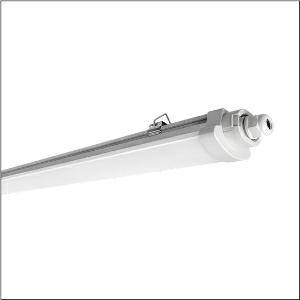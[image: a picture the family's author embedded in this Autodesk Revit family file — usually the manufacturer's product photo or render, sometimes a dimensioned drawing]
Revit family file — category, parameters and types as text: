
# Revit family: monsun_r__41_51fk20mk440a003_a901
name_source: partatom
category: Lighting Fixtures
units: mm (PartAtom-declared; Revit-internal decimal feet)

## family parameters
Cut with Voids When Loaded = No
Host = Face
Light Source = No
Part Type = Normal
Room Calculation Point = No
Round Connector Dimension = Use Diameter
Shared = No

## types (1)
- --- (1 x LED, 4000 lm, 30 W, 4000K)
    Apparent Load = 30 VA
    CIE Flux Codes = 44 74 92 92 100
    Color Rendering = 80
    Color Temperature = 4000K
    Default Elevation = 1800 mm
    Description = Monsun® 41, damp-proof luminaire, primary optical cover: diffuser, of PC, frosted, light emission: direct distribution, primary light characteristic: symmetric, installation type: surface-mounted, suspended mounting, LED, rated luminous flux: 4.000lm, luminous efficacy: 130lm/W, light colour: 840, colour temperature: 4000K, control gear: ECG Multilumen, with terminal, 3-pole, through-wiring: 3x 1.5mm², mains connection: 220..240V, AC, 50/60Hz, rated input power: 30W, housing, luminaire housing, of PC, grey, length: 1.200mm, width: 79mm, height: 52mm, end cap, of PC, grey, ceiling mounting element, of stainless steel (V2A), protection rating (complete): IP65, insulation class (complete): insulation class II (safety insulation), certification: CE, UKCA, protection symbol: D, impact resistance: IK08, permissible operating ambient temperature: -20..+35°C, corresponds to IFS (International Featured Standards) requirements for safety and quality in the food industry, contact your sales advisor before using the luminaires in applications with unclear chemical exposure, large temperature fluctuations or condensation-forming humidity, packaging unit: 1 piece
    Height = 54 mm
    Lamp = 1 x LED
    Lamp Light Flux = 4000 lm
    Lamp Power = 30 W
    Lamp count = 1
    Length = 1200 mm
    Luminous efficacy = 133 lm/W
    Manufacturer = Siteco
    ModVariant = No
    Model = 51FK20MK440A003
    Mounting Place = Ceiling
    Mounting Type = Surface mounted
    Number of Poles = 1
    OnlyDefault = Yes
    Power Factor = 1
    Product Name = Monsun® 41
    Product group = damp-proof luminaire
    ProductGroupID = 300
    Protection Class = Protection class II
    Protection Degree = IP 65
    RLX_Detail_Level = 1
    RLX_Emergency_Light_Flux = 0 lm
    RLX_Emergency_Type = 0
    RLX_Emergency_Type_DB = No
    RlxData = <blob elided: 31877 chars, md5=3ca93f77>
    Socket = socket
    Standby Power = 0 W
    System Light Flux = 4000 lm
    System Power = 30 W
    Type Comments = factory setting: luminous flux: 100 % | (HIGH)
    Type Image = l_1007037.jpg
    URL = http://relux.com
    VarID = @adj_107853
    Voltage = 0 V
    Weight = 0.00 kg
    Width = 79 mm

## geometry (parser evidence)
native form markers: Blend x4, Sweep x11
no freeform markers — native parametric forms only
